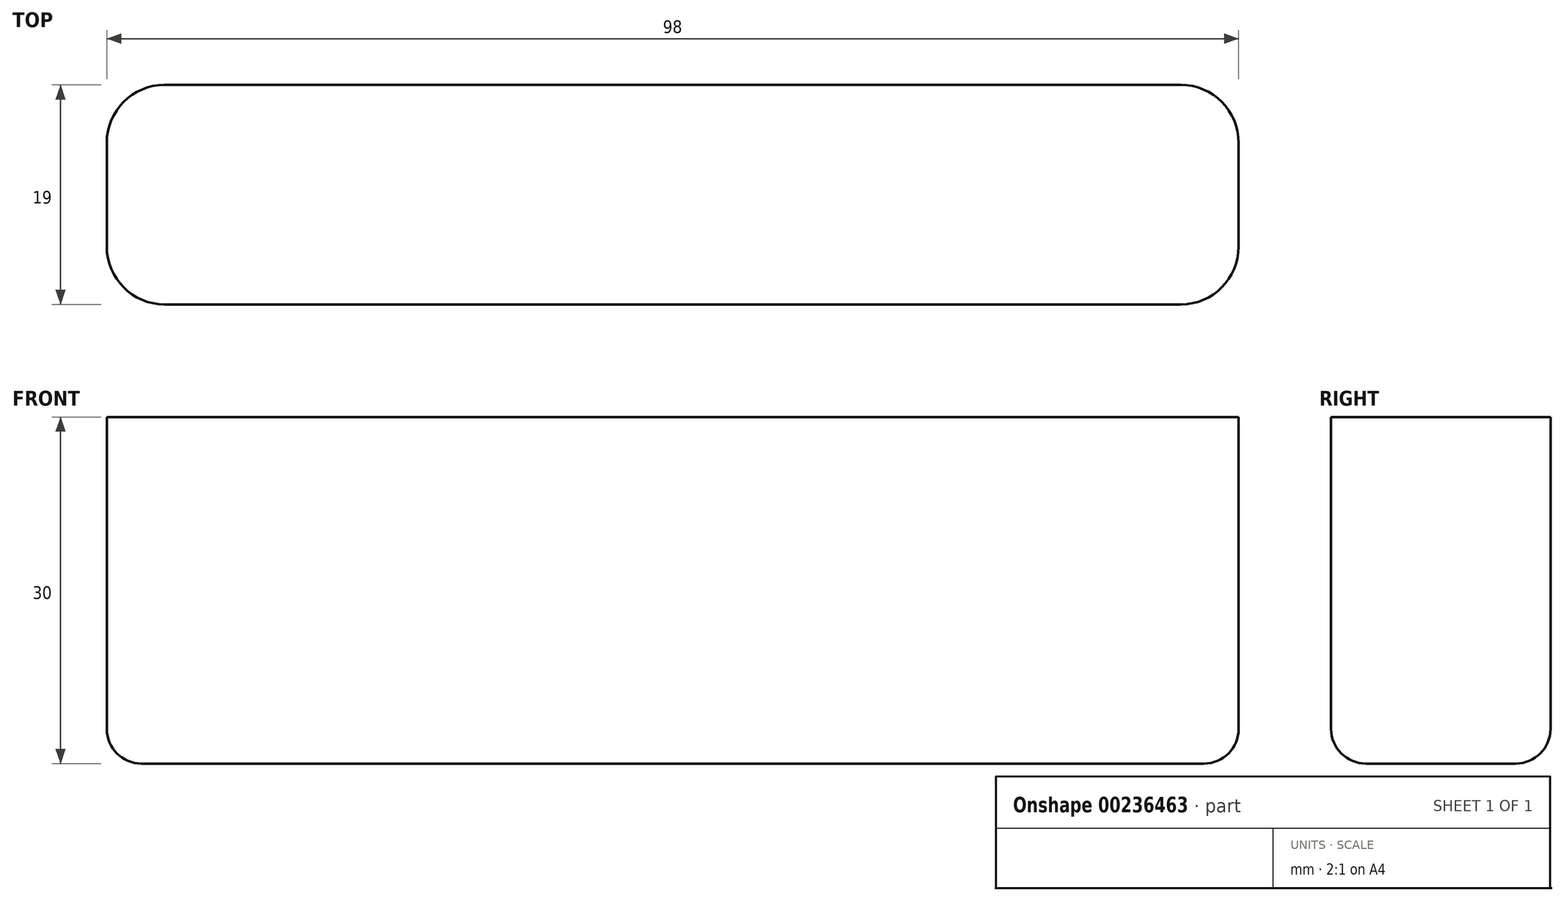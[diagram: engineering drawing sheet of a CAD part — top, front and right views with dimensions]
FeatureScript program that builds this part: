
annotation { "Feature Type Name" : "Feature", "Feature Type Description" : "" }
export const myFeature = defineFeature(function(context is Context, id is Id, definition is map)
    precondition{}
    {
        {
            var Q0;
            Q0=qCreatedBy(makeId("Top.planeOp"),FACE);
            var sketch = newSketch(context, id + "F0", { "sketchPlane" : qUnion([Q0])});
            skLineSegment(sketch, "E0.bottom", {"start": v(44, -9.5) * mm, "end": v(-44, -9.5) * mm});
            skLineSegment(sketch, "E0.top", {"start": v(44, 9.5) * mm, "end": v(-44, 9.5) * mm});
            skLineSegment(sketch, "E0.left", {"start": v(49, -4.5) * mm, "end": v(49, 4.5) * mm});
            skLineSegment(sketch, "E0.right", {"start": v(-49, -4.5) * mm, "end": v(-49, 4.5) * mm});
            skPoint(sketch, "E0.middle", {"position": v(0, 0) * mm});
            skPoint(sketch, "E1.visualSharp", {"position": v(-49, 9.5) * mm});
            skArc(sketch, "E1.filletArc", {"start": v(-44, 9.5) * mm, "mid": v(-47.54, 8.04) * mm, "end": v(-49, 4.5) * mm});
            skPoint(sketch, "E2.visualSharp", {"position": v(49, 9.5) * mm});
            skArc(sketch, "E2.filletArc", {"start": v(49, 4.5) * mm, "mid": v(47.54, 8.04) * mm, "end": v(44, 9.5) * mm});
            skPoint(sketch, "E3.visualSharp", {"position": v(49, -9.5) * mm});
            skArc(sketch, "E3.filletArc", {"start": v(44, -9.5) * mm, "mid": v(47.54, -8.04) * mm, "end": v(49, -4.5) * mm});
            skPoint(sketch, "E4.visualSharp", {"position": v(-49, -9.5) * mm});
            skArc(sketch, "E4.filletArc", {"start": v(-49, -4.5) * mm, "mid": v(-47.54, -8.04) * mm, "end": v(-44, -9.5) * mm});
            skSolve(sketch);
        }
        {
            var Q0;
            Q0=makeQuery(id+"F0.imprint","IMPRINT",FACE,{"disambiguationData":[TD([[makeQuery(id+"F0.imprint","IMPRINT",EDGE,{"derivedFrom":sQuery(id+"F0.wireOp",EDGE,"E0.bottom")}),-1.0]])]});
            extrude(context, id + "F1", {"entities" : qUnion([Q0]), "depth" : 30 * mm});
        }
        {
            var Q0;
            {var subQ0=sQuery(id+"F0.wireOp",EDGE,"39bf8d89-3d3c-4ff3-a256-52f1035d92dd.filletArc");var subQ1=sQuery(id+"F0.wireOp",EDGE,"59a113f9-093f-4c60-8226-30c25c7f52c6.filletArc");var subQ2=sQuery(id+"F0.wireOp",EDGE,"40696cb9-b9db-4bf8-963b-28f77a69f96c.filletArc");var subQ3=sQuery(id+"F0.wireOp",EDGE,"24365927-c618-4868-909a-f2a0cff56809.filletArc");var subQ4=sQuery(id+"F0.wireOp",EDGE,"4vuukDC4-Z9pt-ozC3-fvnZ-XiJCcBOKcEop.right");var subQ5=sQuery(id+"F0.wireOp",EDGE,"4vuukDC4-Z9pt-ozC3-fvnZ-XiJCcBOKcEop.left");var subQ6=sQuery(id+"F0.wireOp",EDGE,"4vuukDC4-Z9pt-ozC3-fvnZ-XiJCcBOKcEop.top");var subQ7=sQuery(id+"F0.wireOp",EDGE,"4vuukDC4-Z9pt-ozC3-fvnZ-XiJCcBOKcEop.bottom");Q0=makeQuery(id+"FqnNAhWJPwV3bhr_1.boolean.opBoolean","MERGE",FACE,{"derivedFrom":[makeQuery(id+"F1.opExtrude","CAP_FACE",FACE,{"disambiguationData":[OSD([sQuery(id+"F0.wireOp",EDGE,"E0.bottom"),sQuery(id+"F0.wireOp",EDGE,"E0.top"),sQuery(id+"F0.wireOp",EDGE,"E0.left"),sQuery(id+"F0.wireOp",EDGE,"E0.right"),sQuery(id+"F0.wireOp",EDGE,"E1.filletArc"),sQuery(id+"F0.wireOp",EDGE,"E2.filletArc"),sQuery(id+"F0.wireOp",EDGE,"E3.filletArc"),sQuery(id+"F0.wireOp",EDGE,"E4.filletArc"),subQ7,subQ6,subQ5,subQ4,subQ3,subQ2,subQ1,subQ0])],"isStart":true}),makeQuery(id+"FqnNAhWJPwV3bhr_1.opExtrude","CAP_FACE",FACE,{"disambiguationData":[OSD([subQ7,subQ6,subQ5,subQ4,subQ3,subQ2,subQ1,subQ0])],"isStart":true})]});}
            fillet(context, id + "F2", {"entities" : qUnion([Q0]), "radius" : 3 * mm, "tangentPropagation" : true, "allowEdgeOverflow" : false});
        }
    });
